# Revit family: FP_107_update-211019
name_source: partatom
category: Doors
units: mm (PartAtom-declared; Revit-internal decimal feet)

## family parameters
Always vertical = Yes
Cut with Voids When Loaded = No
Host = Wall
OmniClass Number = 23.30.10.00
OmniClass Title = Doors
Room Calculation Point = No
Shared = No

## types (15) — shared parameters
Analytic Construction = <None>
Casing Thickness = 0' - 0 3/4"
Center = 0' - 0 7/8"
Define Thermal Properties by = Schematic Type
Door Thickness = 0' - 1 3/4"
Function = Interior
Jamb Thickness = 0' - 0 3/4"
Jamb Width (4 9/16", 4 13/16", 6 9/16", 6 13/16") = 0' - 4 9/16"
Manufacturer = Treely Doors
Panel Thickness = 0' - 0 3/4"
Stop Width = 0' - 1 3/8"
Thickness = 0' - 1 3/4"
URL = www.treelydoors.com
Wall Closure = By host

## per-type parameters (varying)
| type | Casing Material | Height | Jamb Material | Panel Material | Rough Height | Rough Width | Stile Material | Width |
| 2'-0" x 8'-0" | <By Category> | 7' - 0" | <By Category> | <By Category> | 7' - 0 3/4" | 2' - 7 1/2" | <By Category> | 2' - 6" |
| 2'-4" x 8'-0" | <By Category> | 8' - 0" | <By Category> | <By Category> | 8' - 0 3/4" | 2' - 5 1/2" | <By Category> | 2' - 4" |
| 2'-6" x 8'-0" | <By Category> | 8' - 0" | <By Category> | <By Category> | 8' - 0 3/4" | 2' - 7 1/2" | <By Category> | 2' - 6" |
| 2'-8" x 8'-0" | <By Category> | 8' - 0" | <By Category> | <By Category> | 8' - 0 3/4" | 2' - 9 1/2" | <By Category> | 2' - 8" |
| 3'-0" x 6'-8" | <By Category> | 6' - 8" | <By Category> | <By Category> | 6' - 8 3/4" | 3' - 1 1/2" | <By Category> | 3' - 0" |
| 3'-0" x 7'-0" | <By Category> | 7' - 0" | <By Category> | <By Category> | 7' - 0 3/4" | 3' - 1 1/2" | <By Category> | 3' - 0" |
| 3'-0" x 8'-0" | <By Category> | 8' - 0" | <By Category> | <By Category> | 8' - 0 3/4" | 3' - 1 1/2" | <By Category> | 3' - 0" |
| 2'-8" x 7'-0" | <By Category> | 7' - 0" | <By Category> | <By Category> | 7' - 0 3/4" | 2' - 9 1/2" | <By Category> | 2' - 8" |
| 2'-8" x 6'-8" | <By Category> | 6' - 8" | <By Category> | <By Category> | 6' - 8 3/4" | 2' - 9 1/2" | <By Category> | 2' - 8" |
| 2'-6" x 7'-0" | <By Category> | 7' - 0" | <By Category> | <By Category> | 7' - 0 3/4" | 2' - 7 1/2" | <By Category> | 2' - 6" |
| 2'-6" x 6'-8" | <By Category> | 6' - 8" | <By Category> | <By Category> | 6' - 8 3/4" | 2' - 7 1/2" | <By Category> | 2' - 6" |
| 2'-4" x 7'-0" | <By Category> | 7' - 0" | <By Category> | <By Category> | 7' - 0 3/4" | 2' - 5 1/2" | <By Category> | 2' - 4" |
| 2'-4" x 6'-8" | TreelyDoors_Wood_Maple | 6' - 8" | TreelyDoors_Wood_Maple | Glass | 6' - 8 3/4" | 2' - 5 1/2" | TreelyDoors_Wood_Maple | 2' - 4" |
| 2'-0" x 7'-0" | <By Category> | 7' - 0" | <By Category> | <By Category> | 7' - 0 3/4" | 2' - 1 1/2" | <By Category> | 2' - 0" |
| 2'-0" x 6'-8" | <By Category> | 6' - 8" | <By Category> | <By Category> | 6' - 8 3/4" | 2' - 1 1/2" | <By Category> | 2' - 0" |

## geometry (parser evidence)
native form markers: Sweep x2
no freeform markers — native parametric forms only
